# Revit family: 201_ECO3-_
name_source: partatom
category: Air Terminals
units: mm (PartAtom-declared; Revit-internal decimal feet)

## family parameters
Always vertical = Yes
Cut with Voids When Loaded = No
Part Type = Normal
Room Calculation Point = Yes
Round Connector Dimension = Use Diameter
Shared = No
Work Plane-Based = No

## types (1)
- ECO3-125
    A = 255 mm  [stored 0.836614 ft]
    CAT0 = Yes
    CLBTZ = 0 mm  [stored 0 ft]
    CL_Location_5000 = 5000 mm  [stored 16.4042 ft]
    CON1 = Yes
    CON2 = No
    CON3 = No
    CON4 = No
    D = 125 mm
    Description = Room air heating unit. Ceiling mounting. Without control unit
    EX = 60 mm  [stored 0.19685 ft]
    EX__ve = -60 mm  [stored -0.19685 ft]
    H_ARR = 0 mm  [stored 0 ft]
    L1 = 45 mm  [stored 0.147638 ft]
    L_ARR = 400 mm  [stored 1.31234 ft]
    MC Product Code = ECO3-125
    Manufacturer = Climecon
    QmdConnectorList = 201;D
    R = 5 mm  [stored 0.0164042 ft]
    URL = www.climecon.fi
    W_ARR = 400 mm  [stored 1.31234 ft]
    magiPartTypeId = 201
    magiProductFamilyId = ECO3-*
    magiProductId = ECO3-125

note: [stored X ft] marks values corroborated as IEEE doubles in the binary element streams (Revit-internal decimal feet)

## geometry (parser evidence)
native form markers: Sweep x1
no freeform markers — native parametric forms only
